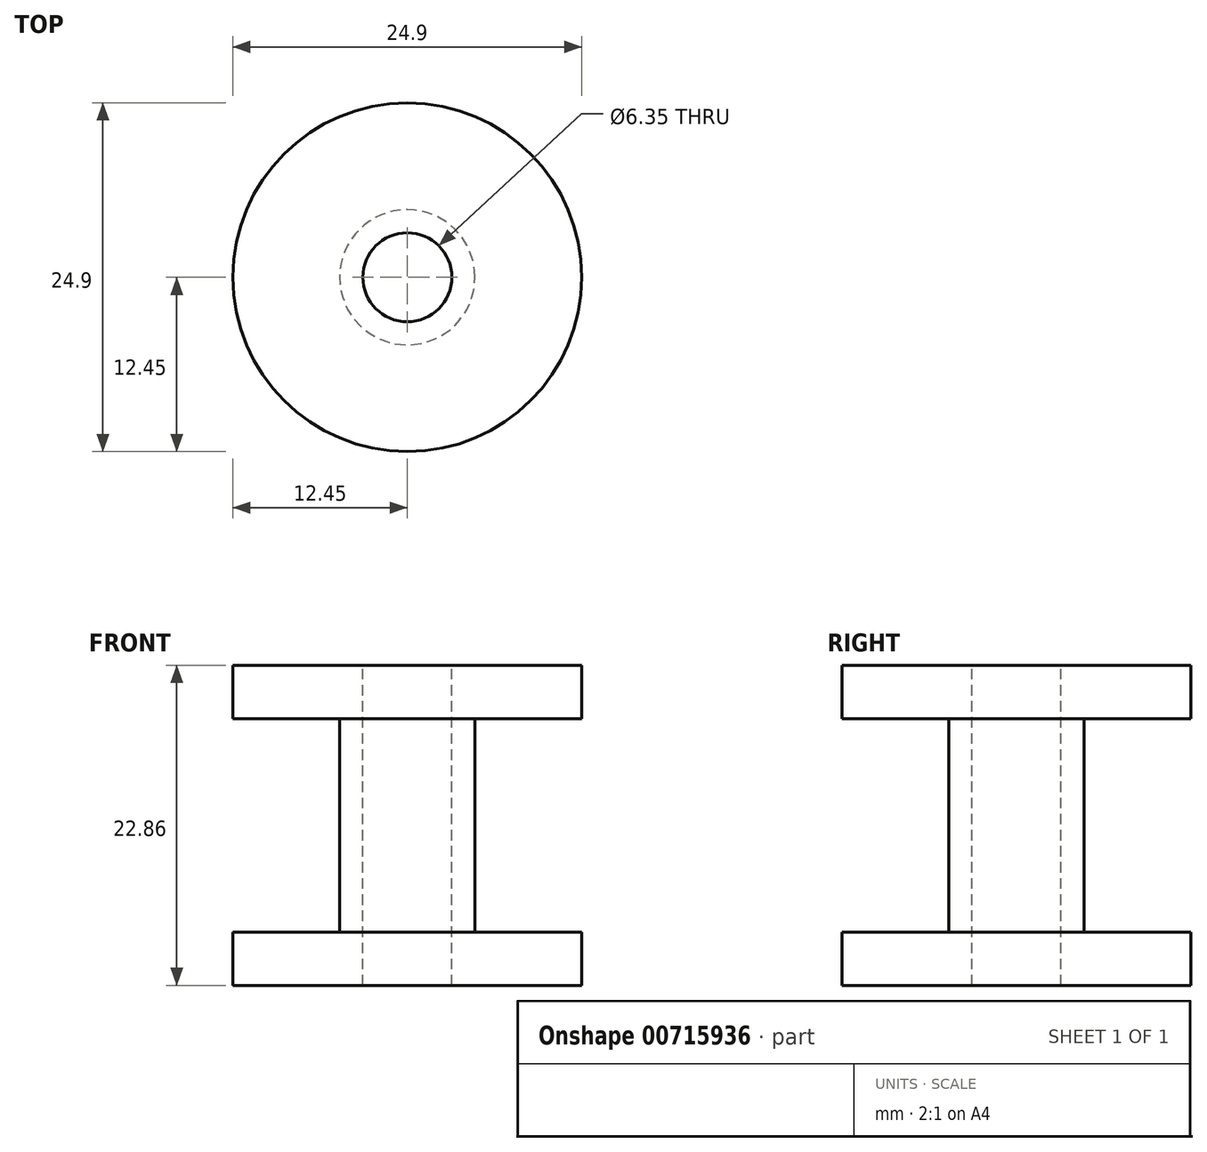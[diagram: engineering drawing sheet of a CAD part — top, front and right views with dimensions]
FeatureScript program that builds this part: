
annotation { "Feature Type Name" : "Feature", "Feature Type Description" : "" }
export const myFeature = defineFeature(function(context is Context, id is Id, definition is map)
    precondition{}
    {
        {
            var Q0;
            Q0=qCreatedBy(makeId("Top.planeOp"),FACE);
            var sketch = newSketch(context, id + "F0", { "sketchPlane" : qUnion([Q0])});
            skCircle(sketch, "E0", {"center": v(0, 0) * mm, "radius": 12.45 * mm});
            skSolve(sketch);
        }
        {
            var Q0;
            Q0=qCreatedBy(makeId("Front.planeOp"),FACE);
            var sketch = newSketch(context, id + "F1", { "sketchPlane" : qUnion([Q0])});
            skLineSegment(sketch, "E1", {"start": v(12.45, 0) * mm, "end": v(12.45, 3.81) * mm});
            skLineSegment(sketch, "E2", {"start": v(12.45, 3.81) * mm, "end": v(4.83, 3.81) * mm});
            skLineSegment(sketch, "E3", {"start": v(4.83, 3.81) * mm, "end": v(4.83, 19.05) * mm});
            skLineSegment(sketch, "E4", {"start": v(4.83, 19.05) * mm, "end": v(12.45, 19.05) * mm});
            skLineSegment(sketch, "E5", {"start": v(12.45, 19.05) * mm, "end": v(12.45, 22.86) * mm});
            skLineSegment(sketch, "E6", {"start": v(12.45, 22.86) * mm, "end": v(0, 22.86) * mm});
            skLineSegment(sketch, "E7", {"start": v(0, 22.86) * mm, "end": v(0, 0) * mm});
            skLineSegment(sketch, "E8", {"start": v(12.45, 0) * mm, "end": v(0, 0) * mm});
            skLineSegment(sketch, "E9", {"start": v(3.18, 0) * mm, "end": v(3.18, 22.86) * mm});
            skSolve(sketch);
        }
        {
            var Q0;
            {var subQ0=sQuery(id+"F1.wireOp",EDGE,"E1");Q0=makeQuery(id+"F1.imprint","IMPRINT",FACE,{"disambiguationData":[TD([[makeQuery(id+"F1.imprint","IMPRINT",EDGE,{"derivedFrom":subQ0}),1.0]])]});}
            var Q1;
            Q1=sQuery(id+"F1.wireOp",EDGE,"E7");
            revolve(context, id + "F2", {"surfaceOperationType" : NewSurfaceOperationType.NEW, "entities" : qUnion([Q0]), "axis" : qUnion([Q1]), "revolveType" : RevolveType.FULL});
        }
    });
